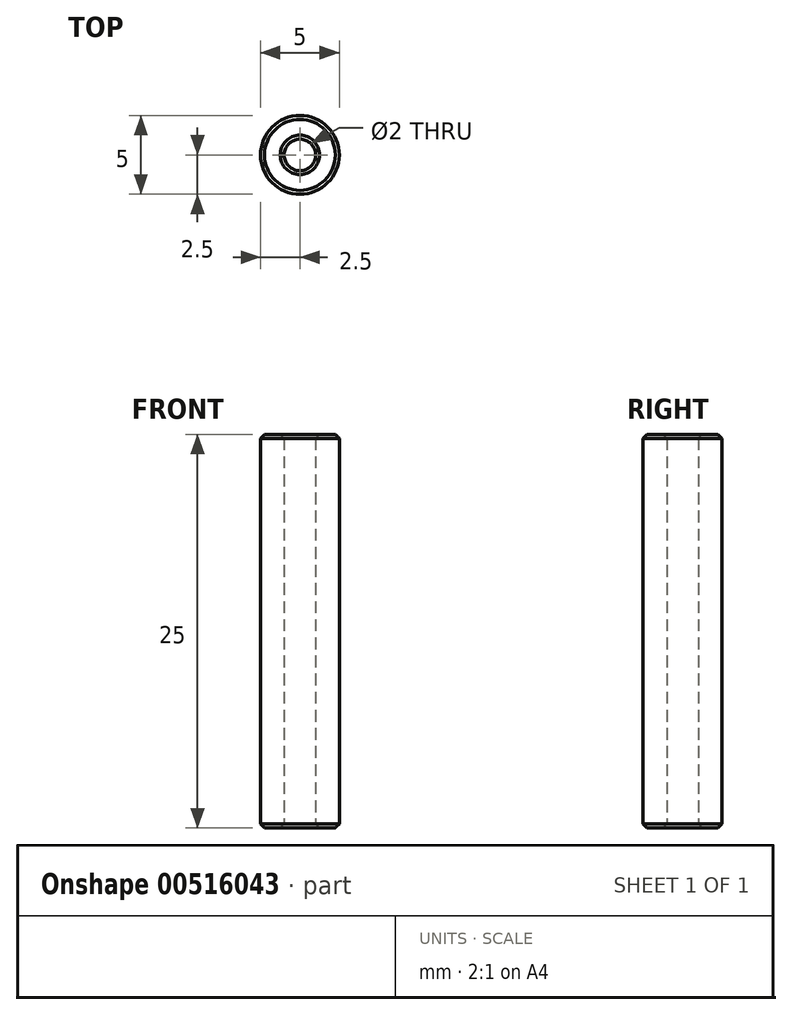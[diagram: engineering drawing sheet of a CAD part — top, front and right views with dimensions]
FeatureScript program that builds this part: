
annotation { "Feature Type Name" : "Feature", "Feature Type Description" : "" }
export const myFeature = defineFeature(function(context is Context, id is Id, definition is map)
    precondition{}
    {
        {
            var Q0;
            Q0=qCreatedBy(makeId("Top.planeOp"),FACE);
            var sketch = newSketch(context, id + "F0", { "sketchPlane" : qUnion([Q0])});
            skCircle(sketch, "E0", {"center": v(0, 0) * mm, "radius": 2.5 * mm});
            skCircle(sketch, "E1", {"center": v(0, 0) * mm, "radius": 1 * mm});
            skSolve(sketch);
        }
        {
            var Q0;
            Q0=qSketchRegion(id+"F0",true);
            extrude(context, id + "F1", {"entities" : qUnion([Q0]), "depth" : 25 * mm, "offsetDistance" : 25 * mm});
        }
        {
            var Q0;
            Q0=makeQuery(id+"F1.opExtrude","CAP_EDGE",EDGE,{"disambiguationData":[OSD([sQuery(id+"F0.wireOp",EDGE,"E0")])],"isStart":false});
            var Q1;
            Q1=makeQuery(id+"F1.opExtrude","CAP_EDGE",EDGE,{"disambiguationData":[OSD([sQuery(id+"F0.wireOp",EDGE,"E0")])],"isStart":true});
            var Q2;
            Q2=makeQuery(id+"F1.opExtrude","CAP_EDGE",EDGE,{"disambiguationData":[OSD([sQuery(id+"F0.wireOp",EDGE,"E1")])],"isStart":false});
            var Q3;
            Q3=makeQuery(id+"F1.opExtrude","CAP_EDGE",EDGE,{"disambiguationData":[OSD([sQuery(id+"F0.wireOp",EDGE,"E1")])],"isStart":true});
            chamfer(context, id + "F2", {"entities" : qUnion([Q0, Q1, Q2, Q3]), "width" : .25 * mm, "tangentPropagation" : true});
        }
    });
